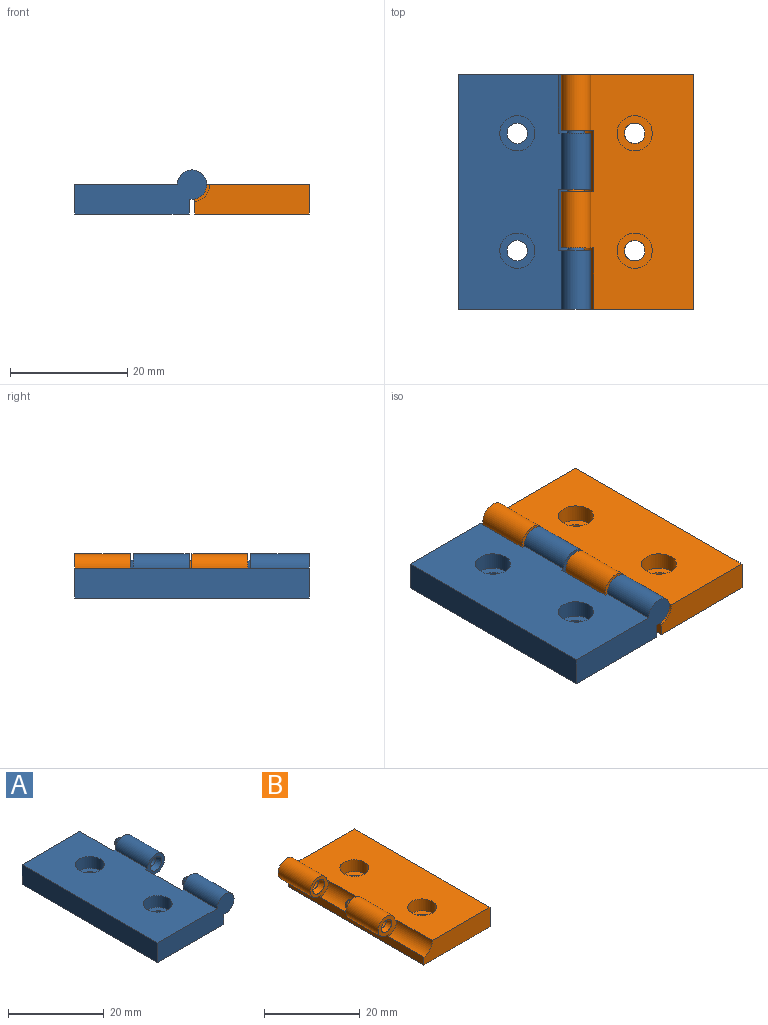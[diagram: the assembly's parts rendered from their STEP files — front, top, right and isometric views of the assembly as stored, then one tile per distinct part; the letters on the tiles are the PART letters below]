
ASSEMBLY  parts=2 mates=1
PART A: 30 faces, bbox 22.5x40x7.5 mm
  f0: plane 40x2.5mm, normal (1,0,0), area 90.6mm2, adj f1,f3,f4,f5,f14,f19,f23,f24
  f1: plane 19.5x5mm, normal (0,1,0), area 91.9mm2, adj f0,f2,f4,f8,f28
  f2: plane 40x17.5mm, normal (0,0,1), area 633.2mm2, adj f1,f5,f8,f11,f12,f13,f14,f18
  f3: plane 9.5x0.5mm, normal (0,0,-1), area 4.8mm2, adj f0,f18,f19,f24
  f4: plane 40x19.5mm, normal (0,0,-1), area 760.8mm2, adj f0,f1,f5,f8,f9,f10
  f5: plane 22.5x7.5mm, normal (0,-1,0), area 113.5mm2, adj f0,f2,f4,f8,f13,f23
  f6: plane 6x6mm, normal (0,0,1), area 18.7mm2, adj f9,f12
  f7: plane 6x6mm, normal (0,0,1), area 18.7mm2, adj f10,f11
  f8: plane 40x5mm, normal (-1,0,0), area 200mm2, adj f1,f2,f4,f5
  f9: cylinder r=1.75mm len=3.5mm, axis (0,0,-1), area 22mm2, adj f4,f6
  f10: cylinder r=1.75mm len=3.5mm, axis (0,0,-1), area 22mm2, adj f4,f7
  f11: cylinder r=3mm len=6mm, axis (0,0,-1), area 56.5mm2, adj f2,f7
  f12: cylinder r=3mm len=6mm, axis (0,0,-1), area 56.5mm2, adj f2,f6
  f13: cylinder r=2.5mm len=10mm, axis (0,-1,0), area 117.8mm2, adj f2,f5,f14,f23
  f14: plane 5.5x5.46mm, normal (0,1,0), area 14.5mm2, adj f0,f2,f13,f15,f23,f29
  f15: cone r=1mm half-angle=18.4deg, axis (0,-1,0), area 12.4mm2, adj f14,f16
  f16: torus R=0.5mm, axis (0,1,0), area 4mm2, adj f15,f17
  f17: plane 1x1mm, normal (0,1,0), area 0.8mm2, adj f16
  f18: cylinder r=2.5mm len=9.5mm, axis (0,-1,0), area 111.9mm2, adj f2,f3,f19,f24
  f19: plane 5.5x5.46mm, normal (0,1,0), area 14.5mm2, adj f0,f2,f3,f18,f20,f28
  f20: cone r=1mm half-angle=18.4deg, axis (0,-1,0), area 12.4mm2, adj f19,f21
  f21: torus R=0.5mm, axis (0,-1,0), area 4mm2, adj f20,f22
  f22: plane 1x1mm, normal (0,1,0), area 0.8mm2, adj f21
  f23: plane 10x0.5mm, normal (0,0,-1), area 5mm2, adj f0,f5,f13,f14
  f24: plane 5.5x5.46mm, normal (0,-1,0), area 12.3mm2, adj f0,f2,f3,f18,f27,f29
  f25: plane 1.15x1.15mm, normal (0,-1,0), area 1mm2, adj f26
  f26: torus R=0.57mm, axis (0,-1,0), area 5.3mm2, adj f25,f27
  f27: cone r=1.15mm half-angle=24.9deg, axis (0,-1,0), area 12.2mm2, adj f24,f26
  f28: cylinder r=3mm len=10mm, axis (0,-1,0), area 42.1mm2, adj f0,f1,f2,f19
  f29: cylinder r=3mm len=10.5mm, axis (0,-1,0), area 44.2mm2, adj f0,f2,f14,f24
PART B: 30 faces, bbox 22.5x40x7.5 mm
  f0: plane 40x17.5mm, normal (0,0,1), area 633mm2, adj f2,f3,f4,f6,f8,f9,f11,f15
  f1: plane 40x2.5mm, normal (-1,0,0), area 90.4mm2, adj f4,f5,f6,f7,f15,f19,f20,f24
  f2: cylinder r=2.5mm len=9.5mm, axis (0,1,0), area 111.9mm2, adj f0,f6,f19,f24
  f3: cylinder r=2.5mm len=9.5mm, axis (0,1,0), area 111.9mm2, adj f0,f5,f15,f20
  f4: plane 19.5x5mm, normal (0,-1,0), area 91.9mm2, adj f0,f1,f7,f8,f28
  f5: plane 9.5x0.5mm, normal (0,0,-1), area 4.8mm2, adj f1,f3,f15,f20
  f6: plane 22.5x7.5mm, normal (0,1,0), area 113.5mm2, adj f0,f1,f2,f7,f8,f19
  f7: plane 40x19.5mm, normal (0,0,-1), area 760.8mm2, adj f1,f4,f6,f8,f13,f14
  f8: plane 40x5mm, normal (1,0,0), area 200mm2, adj f0,f4,f6,f7
  f9: cylinder r=3mm len=6mm, axis (0,0,1), area 56.5mm2, adj f0,f10
  f10: plane 6x6mm, normal (0,0,1), area 18.7mm2, adj f9,f13
  f11: cylinder r=3mm len=6mm, axis (0,0,1), area 56.5mm2, adj f0,f12
  f12: plane 6x6mm, normal (0,0,1), area 18.7mm2, adj f11,f14
  f13: cylinder r=1.75mm len=3.5mm, axis (0,0,1), area 22mm2, adj f7,f10
  f14: cylinder r=1.75mm len=3.5mm, axis (0,0,1), area 22mm2, adj f7,f12
  f15: plane 5.5x5.46mm, normal (0,1,0), area 14.5mm2, adj f0,f1,f3,f5,f16,f29
  f16: cone r=1mm half-angle=18.4deg, axis (0,-1,0), area 12.4mm2, adj f15,f17
  f17: torus R=0.5mm, axis (0,-1,0), area 4mm2, adj f16,f18
  f18: plane 1x1mm, normal (0,1,0), area 0.8mm2, adj f17
  f19: plane 9.5x0.5mm, normal (0,0,-1), area 4.8mm2, adj f1,f2,f6,f24
  f20: plane 5.5x5.46mm, normal (0,-1,0), area 14.4mm2, adj f0,f1,f3,f5,f23,f28
  f21: plane 1.15x1.15mm, normal (0,-1,0), area 1mm2, adj f22
  f22: torus R=0.57mm, axis (0,1,0), area 5.3mm2, adj f21,f23
  f23: cone r=1.15mm half-angle=16.2deg, axis (0,-1,0), area 10.6mm2, adj f20,f22
  f24: plane 5.5x5.46mm, normal (0,-1,0), area 12.3mm2, adj f0,f1,f2,f19,f27,f29
  f25: plane 1.15x1.15mm, normal (0,-1,0), area 1mm2, adj f26
  f26: torus R=0.57mm, axis (0,-1,0), area 5.3mm2, adj f25,f27
  f27: cone r=1.15mm half-angle=24.9deg, axis (0,-1,0), area 12.2mm2, adj f24,f26
  f28: cylinder r=3mm len=10.5mm, axis (0,-1,0), area 44.2mm2, adj f0,f1,f4,f20
  f29: cylinder r=3mm len=10.5mm, axis (0,-1,0), area 44.2mm2, adj f0,f1,f15,f24
PLACE A t=(25,0,0)mm fixed
PLACE B rot(axis=(0,1,0),0deg) t=(0,0,0)mm
MATE revolute B.f3 <-> A.f13  axis (0,1,0) through (45,40,5)mm
